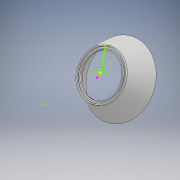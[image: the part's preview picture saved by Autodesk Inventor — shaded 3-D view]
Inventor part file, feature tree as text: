
AUTODESK INVENTOR PART (.ipt)
format: ipt  version: 2018 (Build 220112000, 112)  size: 201,216 bytes
history: native  units: mm
features: sketch x3, revolve x1
ambient origin geometry x8: Origin, YZ Plane, XZ Plane, XY Plane, X Axis, Y Axis, Z Axis, Center Point
bodies: Body1 (feature_tree)
feature tree (4):
  sketch  "Sketch68"  dims[d600=1.4mm d601=2.7mm]
  sketch  "Sketch184"  dims[d604=180.0deg]
  revolve  "Revolution5"  [1 undecoded]
  sketch  "Sketch213"  dims[d21=1.0mm d22=1.0mm]
note: 1 required parameter value undecoded (feature->parameter linkage not recoverable at this tier; creation-order binding heuristic only, values carry confidence <= 0.55)
